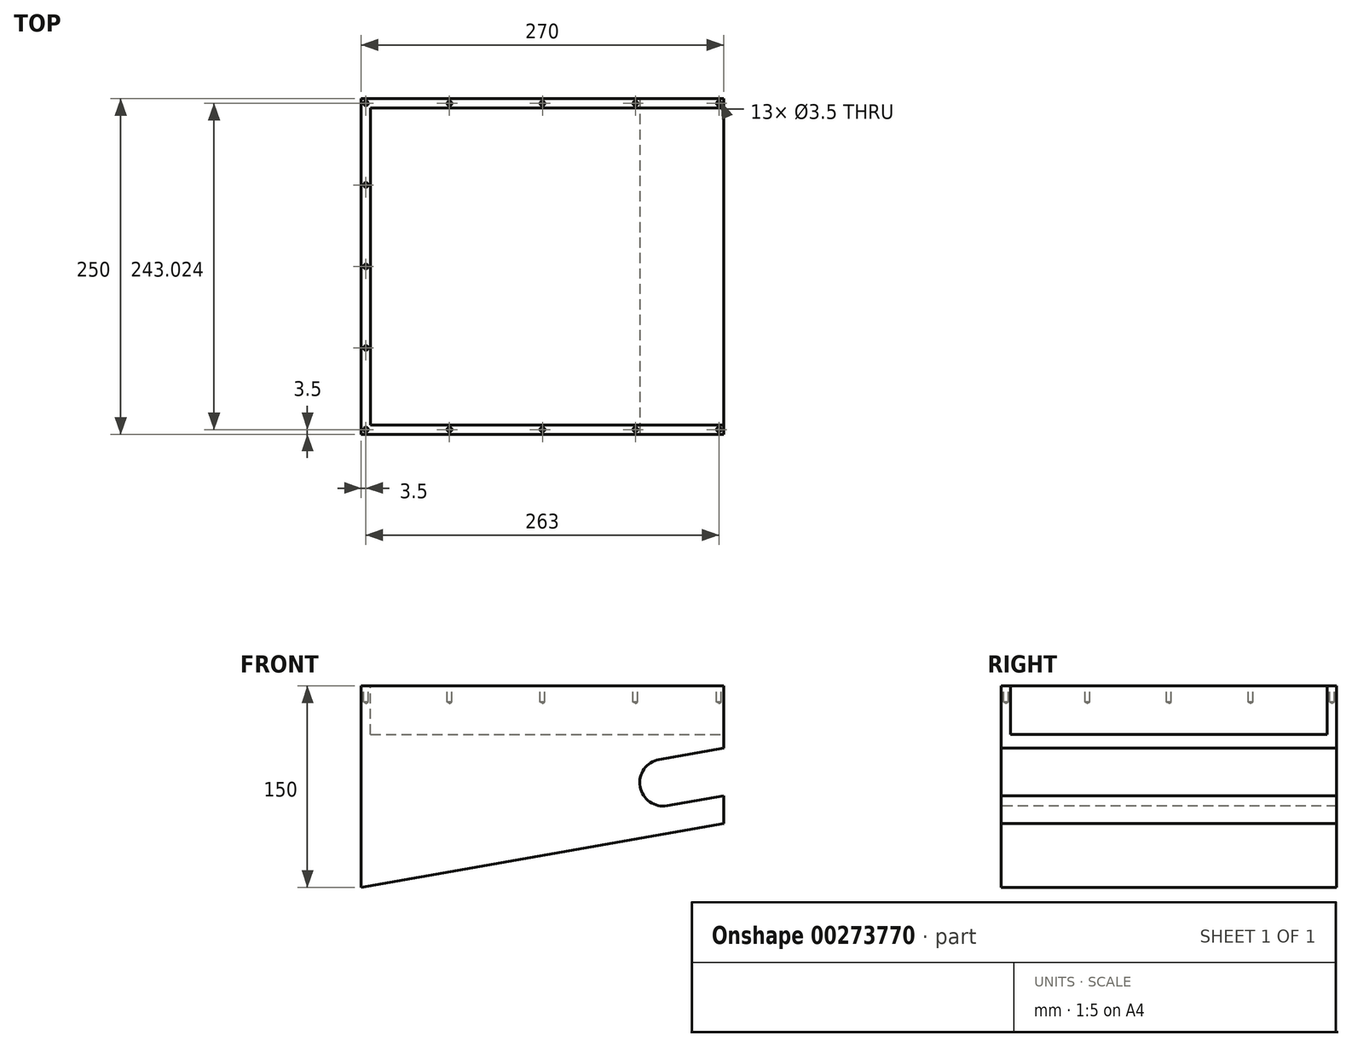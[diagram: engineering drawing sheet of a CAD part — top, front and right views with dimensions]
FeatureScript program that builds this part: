
annotation { "Feature Type Name" : "Feature", "Feature Type Description" : "" }
export const myFeature = defineFeature(function(context is Context, id is Id, definition is map)
    precondition{}
    {
        {
            var Q0;
            Q0=qCreatedBy(makeId("Top.planeOp"),FACE);
            var sketch = newSketch(context, id + "F0", { "sketchPlane" : qUnion([Q0])});
            skLineSegment(sketch, "E0.bottom", {"start": v(0, 0) * mm, "end": v(270, 0) * mm});
            skLineSegment(sketch, "E0.top", {"start": v(0, 250) * mm, "end": v(270, 250) * mm});
            skLineSegment(sketch, "E0.left", {"start": v(0, 0) * mm, "end": v(0, 250) * mm});
            skLineSegment(sketch, "E0.right", {"start": v(270, 0) * mm, "end": v(270, 250) * mm});
            skSolve(sketch);
        }
        {
            var Q0;
            Q0=qCreatedBy(makeId("Top.planeOp"),FACE);
            cPlane(context, id + "F1", {"entities" : qUnion([Q0]), "cplaneType" : CPlaneType.OFFSET, "offset" : 150 * mm, "oppositeDirection" : true, "width" : 150 * mm, "height" : 150 * mm});
        }
        {
            var Q0;
            Q0=qCreatedBy(id+"F1.planeOp",FACE);
            var sketch = newSketch(context, id + "F2", { "sketchPlane" : qUnion([Q0])});
            skLineSegment(sketch, "E1", {"start": v(0, -69.45) * mm, "end": v(0, 279.92) * mm});
            skSolve(sketch);
        }
        {
            var Q0;
            Q0=sQuery(id+"F2.wireOp",EDGE,"E1");
            cPlane(context, id + "F3", {"entities" : qUnion([Q0]), "cplaneType" : CPlaneType.LINE_ANGLE, "offset" : 25 * mm, "angle" : 10 * degree, "oppositeDirection" : true, "width" : 150 * mm, "height" : 150 * mm});
        }
        {
            var Q0;
            Q0=makeQuery(id+"F0.imprint","IMPRINT",FACE,{"disambiguationData":[TD([[makeQuery(id+"F0.imprint","IMPRINT",EDGE,{"derivedFrom":sQuery(id+"F0.wireOp",EDGE,"E0.bottom")}),1.0]])]});
            var Q1;
            Q1=qCreatedBy(id+"F3.planeOp",FACE);
            extrude(context, id + "F4", {"entities" : qUnion([Q0]), "endBound" : BoundingType.UP_TO_SURFACE, "oppositeDirection" : true, "endBoundEntityFace" : qUnion([Q1]), "depth" : 25 * mm});
        }
        {
            var Q0;
            Q0=makeQuery(id+"F4.opExtrude","CAP_FACE",FACE,{"disambiguationData":[OSD([sQuery(id+"F0.wireOp",EDGE,"E0.bottom"),sQuery(id+"F0.wireOp",EDGE,"E0.top"),sQuery(id+"F0.wireOp",EDGE,"E0.left"),sQuery(id+"F0.wireOp",EDGE,"E0.right")])],"isStart":true});
            var sketch = newSketch(context, id + "F5", { "sketchPlane" : qUnion([Q0])});
            skLineSegment(sketch, "E2.bottom", {"start": v(7, 243) * mm, "end": v(270, 243) * mm});
            skLineSegment(sketch, "E2.top", {"start": v(7, 7) * mm, "end": v(270, 7) * mm});
            skLineSegment(sketch, "E2.left", {"start": v(7, 243) * mm, "end": v(7, 7) * mm});
            skLineSegment(sketch, "E2.right", {"start": v(270, 243) * mm, "end": v(270, 7) * mm});
            skSolve(sketch);
        }
        {
            var Q0;
            Q0=makeQuery(id+"F5.imprint","IMPRINT",FACE,{"disambiguationData":[TD([[makeQuery(id+"F5.imprint","IMPRINT",EDGE,{"derivedFrom":sQuery(id+"F5.wireOp",EDGE,"E2.bottom")}),-1.0]])]});
            extrude(context, id + "F6", {"entities" : qUnion([Q0]), "operationType" : NewBodyOperationType.REMOVE, "oppositeDirection" : true, "depth" : 36 * mm});
        }
        {
            var Q0;
            Q0=makeQuery(id+"F4.opExtrude","SWEPT_FACE",FACE,{"disambiguationData":[OSD([sQuery(id+"F0.wireOp",EDGE,"E0.bottom")])]});
            var sketch = newSketch(context, id + "F7", { "sketchPlane" : qUnion([Q0])});
            skArc(sketch, "E3", {"start": v(221.96, -54.77) * mm, "mid": v(207.77, -75.04) * mm, "end": v(228.04, -89.23) * mm});
            skLineSegment(sketch, "E4", {"start": v(228.04, -89.23) * mm, "end": v(270, -81.84) * mm});
            skLineSegment(sketch, "E5", {"start": v(221.96, -54.77) * mm, "end": v(270, -46.3) * mm});
            skLineSegment(sketch, "E6", {"start": v(270, -46.3) * mm, "end": v(270, -81.84) * mm});
            skSolve(sketch);
        }
        {
            var Q0;
            Q0=makeQuery(id+"F7.imprint","IMPRINT",FACE,{"disambiguationData":[TD([[makeQuery(id+"F7.imprint","IMPRINT",EDGE,{"derivedFrom":sQuery(id+"F7.wireOp",EDGE,"E3")}),1.0]])]});
            var Q1;
            Q1=sQuery(id+"F7.wireOp",EDGE,"E5");
            var Q2;
            Q2=sQuery(id+"F7.wireOp",EDGE,"E3");
            var Q3;
            Q3=sQuery(id+"F7.wireOp",EDGE,"E4");
            var Q4;
            Q4=sQuery(id+"F7.wireOp",EDGE,"E6");
            extrude(context, id + "F8", {"entities" : qUnion([Q0]), "operationType" : NewBodyOperationType.REMOVE, "surfaceEntities" : qUnion([Q1, Q2, Q3, Q4]), "endBound" : BoundingType.THROUGH_ALL, "oppositeDirection" : true, "depth" : 25 * mm});
        }
        {
            var Q0;
            Q0=makeQuery(id+"F4.opExtrude","CAP_FACE",FACE,{"disambiguationData":[OSD([sQuery(id+"F0.wireOp",EDGE,"E0.bottom"),sQuery(id+"F0.wireOp",EDGE,"E0.top"),sQuery(id+"F0.wireOp",EDGE,"E0.left"),sQuery(id+"F0.wireOp",EDGE,"E0.right")])],"isStart":true});
            var sketch = newSketch(context, id + "F9", { "sketchPlane" : qUnion([Q0])});
            skPoint(sketch, "E7", {"position": v(65.75, 3.5) * mm});
            skPoint(sketch, "E8", {"position": v(3.5, 3.5) * mm});
            skPoint(sketch, "E9", {"position": v(3.5, 64.25) * mm});
            skPoint(sketch, "E10", {"position": v(3.5, 125) * mm});
            skPoint(sketch, "E11", {"position": v(3.5, 246.5) * mm});
            skPoint(sketch, "E12", {"position": v(3.5, 185.75) * mm});
            skPoint(sketch, "E13", {"position": v(135, 3.5) * mm});
            skPoint(sketch, "E14", {"position": v(135, 246.52) * mm});
            skPoint(sketch, "E15.MirrorP", {"position": v(65.75, 246.5) * mm});
            skPoint(sketch, "E16.MirrorP", {"position": v(204.25, 246.52) * mm});
            skPoint(sketch, "E17.MirrorP", {"position": v(266.5, 246.52) * mm});
            skPoint(sketch, "E18.MirrorP", {"position": v(266.5, 3.5) * mm});
            skPoint(sketch, "E19.MirrorP", {"position": v(204.25, 3.5) * mm});
            skSolve(sketch);
        }
        {
            var Q0;
            Q0=sQuery(id+"F9.wireOp",VERTEX,"E9");
            var Q1;
            Q1=sQuery(id+"F9.wireOp",VERTEX,"E10");
            var Q2;
            Q2=sQuery(id+"F9.wireOp",VERTEX,"E12");
            var Q3;
            Q3=sQuery(id+"F9.wireOp",VERTEX,"E11");
            var Q4;
            Q4=sQuery(id+"F9.wireOp",VERTEX,"E8");
            var Q5;
            Q5=sQuery(id+"F9.wireOp",VERTEX,"E7");
            var Q6;
            Q6=sQuery(id+"F9.wireOp",VERTEX,"E13");
            var Q7;
            Q7=sQuery(id+"F9.wireOp",VERTEX,"E19.MirrorP");
            var Q8;
            Q8=sQuery(id+"F9.wireOp",VERTEX,"E18.MirrorP");
            var Q9;
            Q9=sQuery(id+"F9.wireOp",VERTEX,"E17.MirrorP");
            var Q10;
            Q10=sQuery(id+"F9.wireOp",VERTEX,"E16.MirrorP");
            var Q11;
            Q11=sQuery(id+"F9.wireOp",VERTEX,"E14");
            var Q12;
            Q12=sQuery(id+"F9.wireOp",VERTEX,"E15.MirrorP");
            var Q13;
            Q13=makeQuery(id+"F4.opExtrude","SWEPT_BODY",BODY,{"disambiguationData":[OSD([sQuery(id+"F0.wireOp",EDGE,"E0.bottom"),sQuery(id+"F0.wireOp",EDGE,"E0.top"),sQuery(id+"F0.wireOp",EDGE,"E0.left"),sQuery(id+"F0.wireOp",EDGE,"E0.right")])]});
            hole(context, id + "F10", {"style" : HoleStyle.SIMPLE, "endStyle" : HoleEndStyle.BLIND, "standardTappedOrClearance" : lookupTablePath({ "standard" : "ISO", "size" : "3.5", "type" : "Drilled" }), "standardBlindInLast" : lookupTablePath({ "standard" : "ISO", "size" : "3.5", "type" : "Drilled" }), "holeDiameter" : 3.5 * mm, "holeDepth" : 12 * mm, "tappedDepth" : 12 * mm, "tapClearance" : 3, "locations" : qUnion([Q0, Q1, Q2, Q3, Q4, Q5, Q6, Q7, Q8, Q9, Q10, Q11, Q12]), "scope" : qUnion([Q13])});
        }
    });
